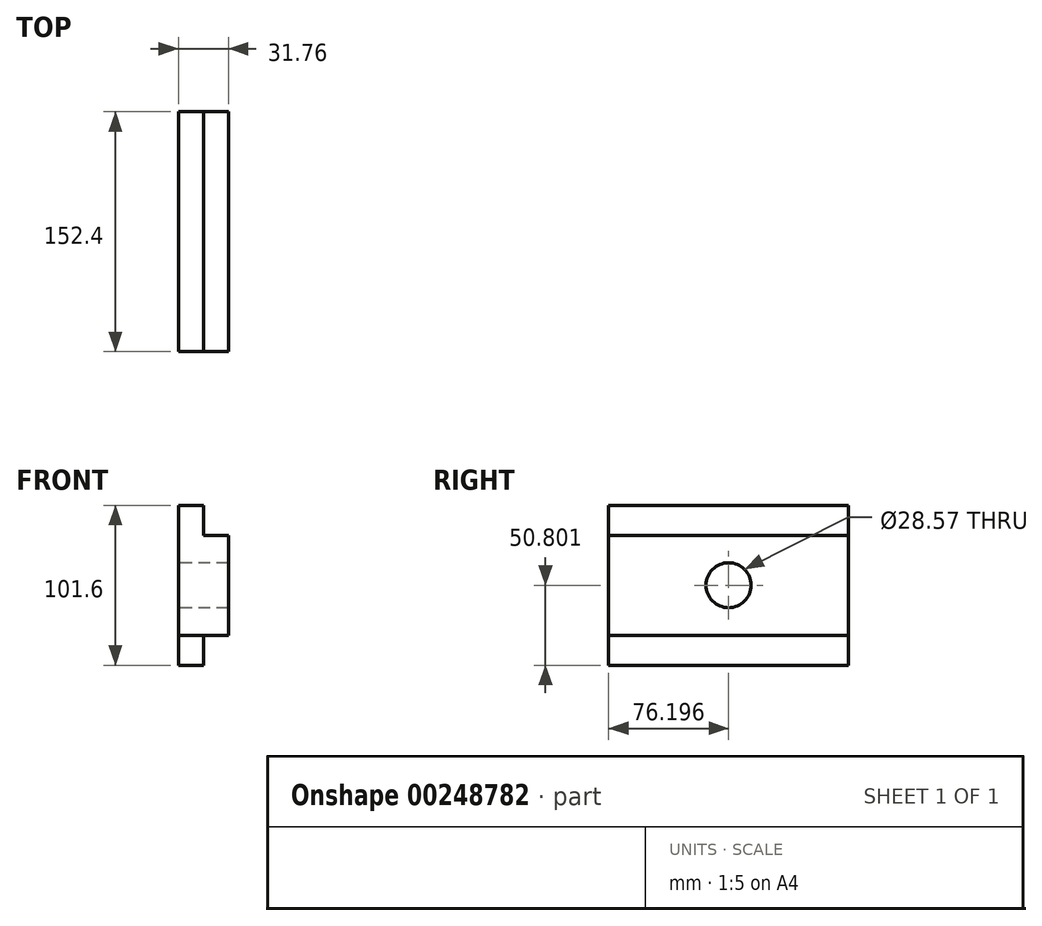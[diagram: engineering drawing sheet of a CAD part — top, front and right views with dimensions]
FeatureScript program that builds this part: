
annotation { "Feature Type Name" : "Feature", "Feature Type Description" : "" }
export const myFeature = defineFeature(function(context is Context, id is Id, definition is map)
    precondition{}
    {
        {
            var Q0;
            Q0=qCreatedBy(makeId("Right.planeOp"),FACE);
            var sketch = newSketch(context, id + "F0", { "sketchPlane" : qUnion([Q0])});
            skLineSegment(sketch, "E0", {"start": v(-75.7, 32.31) * mm, "end": v(-75.7, -31.19) * mm});
            skLineSegment(sketch, "E1", {"start": v(-75.7, -31.19) * mm, "end": v(76.7, -31.19) * mm});
            skLineSegment(sketch, "E2", {"start": v(76.7, -31.19) * mm, "end": v(76.7, 32.31) * mm});
            skLineSegment(sketch, "E3", {"start": v(76.7, 32.31) * mm, "end": v(-75.7, 32.31) * mm});
            skLineSegment(sketch, "E4", {"start": v(-75.7, -31.19) * mm, "end": v(-75.7, -50.24) * mm});
            skLineSegment(sketch, "E5", {"start": v(-75.7, -50.24) * mm, "end": v(76.7, -50.24) * mm});
            skLineSegment(sketch, "E6", {"start": v(76.7, -50.24) * mm, "end": v(76.7, -31.19) * mm});
            skLineSegment(sketch, "E7", {"start": v(-75.7, 32.31) * mm, "end": v(-75.7, 51.36) * mm});
            skLineSegment(sketch, "E8", {"start": v(-75.7, 51.36) * mm, "end": v(76.7, 51.36) * mm});
            skLineSegment(sketch, "E9", {"start": v(76.7, 51.36) * mm, "end": v(76.7, 32.31) * mm});
            skPoint(sketch, "E10", {"position": v(0.5, 0.56) * mm});
            skCircle(sketch, "E11", {"center": v(0.5, 0.56) * mm, "radius": 14.29 * mm});
            skPoint(sketch, "E12.orphan", {"position": v(-75.7, 0.56) * mm});
            skPoint(sketch, "E13.end.orphan", {"position": v(76.7, 0.56) * mm});
            skSolve(sketch);
        }
        {
            var Q0;
            {var subQ5=sQuery(id+"F0.wireOp",EDGE,"E3");Q0=makeQuery(id+"F0.imprint","IMPRINT",FACE,{"disambiguationData":[TD([[makeQuery(id+"F0.imprint","IMPRINT",EDGE,{"derivedFrom":subQ5}),1.0]])]});}
            extrude(context, id + "F1", {"entities" : qUnion([Q0]), "depth" : 15.88 * mm});
        }
        {
            var Q0;
            {var subQ7=sQuery(id+"F0.wireOp",EDGE,"E1");Q0=makeQuery(id+"F0.imprint","IMPRINT",FACE,{"disambiguationData":[TD([[makeQuery(id+"F0.imprint","IMPRINT",EDGE,{"derivedFrom":subQ7}),1.0]])]});}
            var Q1;
            Q1=makeQuery(id+"F0.imprint","IMPRINT",FACE,{"disambiguationData":[TD([[makeQuery(id+"F0.imprint","IMPRINT",EDGE,{"derivedFrom":sQuery(id+"F0.wireOp",EDGE,"E3")}),-1.0]])]});
            extrude(context, id + "F2", {"entities" : qUnion([Q0, Q1]), "operationType" : NewBodyOperationType.ADD, "oppositeDirection" : true, "depth" : 15.88 * mm});
        }
        {
            var Q0;
            {var subQ5=sQuery(id+"F0.wireOp",EDGE,"E3");Q0=makeQuery(id+"F0.imprint","IMPRINT",FACE,{"disambiguationData":[TD([[makeQuery(id+"F0.imprint","IMPRINT",EDGE,{"derivedFrom":subQ5}),1.0]])]});}
            extrude(context, id + "F3", {"entities" : qUnion([Q0]), "oppositeDirection" : true, "depth" : 15.88 * mm});
        }
        {
            var Q0;
            {var subQ7=sQuery(id+"F0.wireOp",EDGE,"E1");Q0=makeQuery(id+"F0.imprint","IMPRINT",FACE,{"disambiguationData":[TD([[makeQuery(id+"F0.imprint","IMPRINT",EDGE,{"derivedFrom":subQ7}),1.0]])]});}
            extrude(context, id + "F4", {"entities" : qUnion([Q0]), "depth" : 5 / 203.2 * mm});
        }
        {
            var Q0;
            Q0=makeQuery(id+"F0.imprint","IMPRINT",FACE,{"disambiguationData":[TD([[makeQuery(id+"F0.imprint","IMPRINT",EDGE,{"derivedFrom":sQuery(id+"F0.wireOp",EDGE,"E1")}),-1.0]])]});
            extrude(context, id + "F5", {"entities" : qUnion([Q0]), "oppositeDirection" : true, "depth" : 15.88 * mm});
        }
        {
            var Q0;
            Q0=makeQuery(id+"F3.opExtrude","SWEPT_BODY",BODY,{"disambiguationData":[OSD([sQuery(id+"F0.wireOp",EDGE,"E0"),sQuery(id+"F0.wireOp",EDGE,"E1"),sQuery(id+"F0.wireOp",EDGE,"E2"),sQuery(id+"F0.wireOp",EDGE,"E3"),sQuery(id+"F0.wireOp",EDGE,"E11")])]});
            deleteBodies(context, id + "F6", {"entities" : qUnion([Q0])});
        }
        {
            var Q0;
            Q0=makeQuery(id+"F4.opExtrude","SWEPT_BODY",BODY,{"disambiguationData":[OSD([sQuery(id+"F0.wireOp",EDGE,"E0"),sQuery(id+"F0.wireOp",EDGE,"E1"),sQuery(id+"F0.wireOp",EDGE,"E2"),sQuery(id+"F0.wireOp",EDGE,"E3"),sQuery(id+"F0.wireOp",EDGE,"E11")])]});
            deleteBodies(context, id + "F7", {"entities" : qUnion([Q0])});
        }
    });
